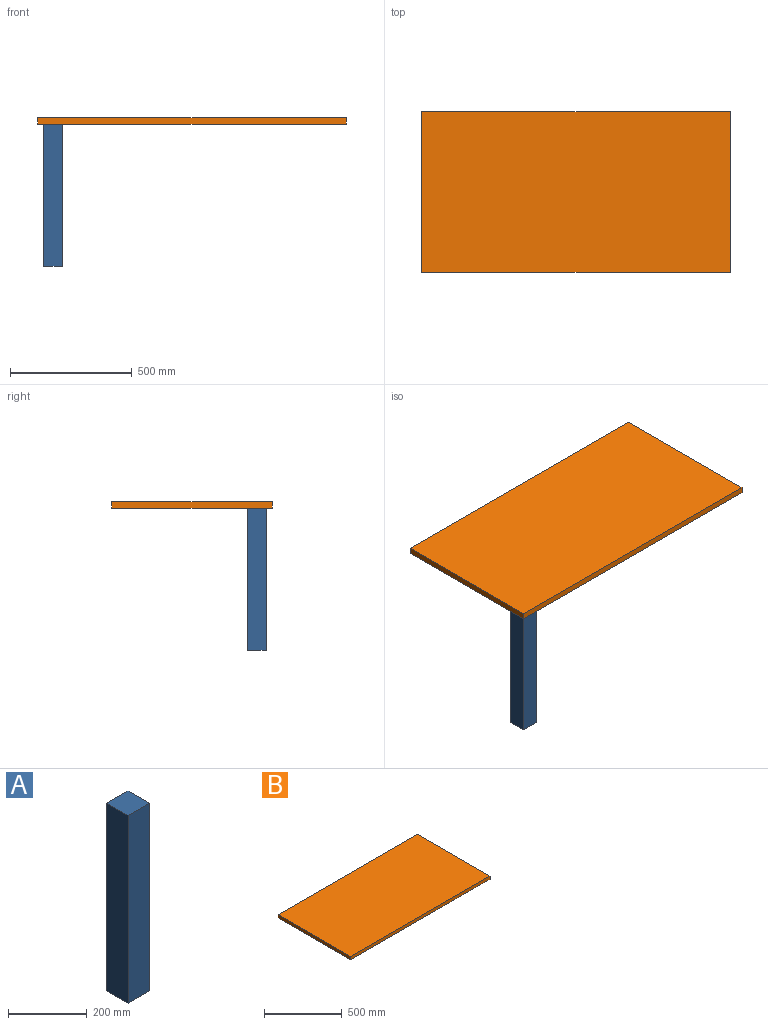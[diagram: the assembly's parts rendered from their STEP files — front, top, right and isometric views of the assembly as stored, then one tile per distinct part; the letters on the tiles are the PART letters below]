
ASSEMBLY  parts=2 mates=1
PART A: 6 faces, bbox 76.2x76.2x584.2 mm
  f0: plane 584.2x76.2mm, normal (1,0,0), area 44516mm2, adj f1,f3,f4,f5
  f1: plane 584.2x76.2mm, normal (0,1,0), area 44516mm2, adj f0,f2,f4,f5
  f2: plane 584.2x76.2mm, normal (-1,0,0), area 44516mm2, adj f1,f3,f4,f5
  f3: plane 584.2x76.2mm, normal (0,-1,0), area 44516mm2, adj f0,f2,f4,f5
  f4: plane 76.2x76.2mm, normal (0,0,-1), area 5806.4mm2, adj f0,f1,f2,f3
  f5: plane 76.2x76.2mm, normal (0,0,1), area 5806.4mm2, adj f0,f1,f2,f3
PART B: 6 faces, bbox 1270x660.4x25.4 mm
  f0: plane 1270x25.4mm, normal (0,1,0), area 32258mm2, adj f1,f3,f4,f5
  f1: plane 660.4x25.4mm, normal (-1,0,0), area 16774.2mm2, adj f0,f2,f4,f5
  f2: plane 1270x25.4mm, normal (0,-1,0), area 32258mm2, adj f1,f3,f4,f5
  f3: plane 660.4x25.4mm, normal (1,0,0), area 16774.2mm2, adj f0,f2,f4,f5
  f4: plane 1270x660.4mm, normal (0,0,1), area 838708mm2, adj f0,f1,f2,f3
  f5: plane 1270x660.4mm, normal (0,0,-1), area 838708mm2, adj f0,f1,f2,f3
PLACE A t=(-597.23,-290.73,-16.1)mm
PLACE B t=(-25.73,-24.03,-3.4)mm
MATE planar B.f5 <-> A.f5  axis (0,0,-1) through (-660.73,-354.23,-16.1)mm
